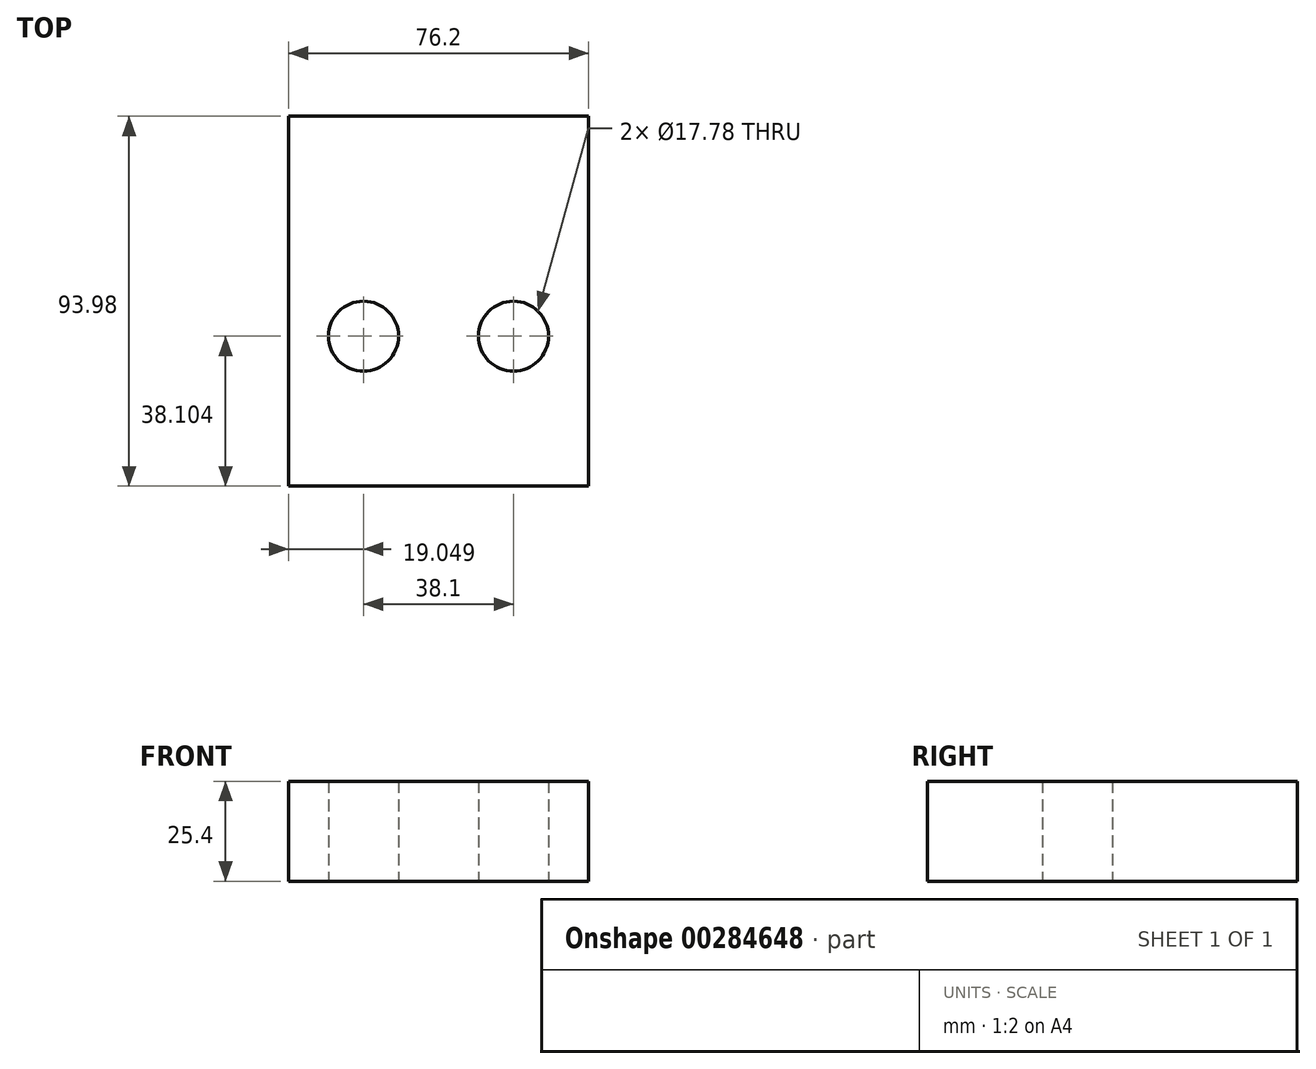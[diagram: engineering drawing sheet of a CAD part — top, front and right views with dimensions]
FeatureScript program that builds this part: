
annotation { "Feature Type Name" : "Feature", "Feature Type Description" : "" }
export const myFeature = defineFeature(function(context is Context, id is Id, definition is map)
    precondition{}
    {
        {
            var Q0;
            Q0=qCreatedBy(makeId("Top.planeOp"),FACE);
            var sketch = newSketch(context, id + "F0", { "sketchPlane" : qUnion([Q0])});
            skLineSegment(sketch, "E0", {"start": v(-41.9, 19.86) * mm, "end": v(-41.9, -56.34) * mm});
            skLineSegment(sketch, "E1", {"start": v(-41.9, -56.34) * mm, "end": v(34.3, -56.34) * mm});
            skLineSegment(sketch, "E2", {"start": v(34.3, -56.34) * mm, "end": v(34.3, 19.86) * mm});
            skLineSegment(sketch, "E3", {"start": v(34.3, 19.86) * mm, "end": v(-41.9, 19.86) * mm});
            skLineSegment(sketch, "E4", {"start": v(34.3, 19.86) * mm, "end": v(34.3, 37.64) * mm});
            skLineSegment(sketch, "E5", {"start": v(34.3, 37.64) * mm, "end": v(-41.9, 37.64) * mm});
            skLineSegment(sketch, "E6", {"start": v(-41.9, 37.64) * mm, "end": v(-41.9, 19.86) * mm});
            skPoint(sketch, "E7.endSnap0", {"position": v(34.3, -18.24) * mm});
            skCircle(sketch, "E8", {"center": v(-22.84, -18.24) * mm, "radius": 8.9 * mm});
            skCircle(sketch, "E9", {"center": v(15.26, -18.24) * mm, "radius": 8.9 * mm});
            skPoint(sketch, "E7.start.orphan", {"position": v(34.3, -18.24) * mm});
            skSolve(sketch);
        }
        {
            var Q0;
            Q0 = qSketchRegion(id + "F0", true);
            extrude(context, id + "F1", {"entities" : qUnion([Q0]), "depth" : 25.4 * mm});
        }
    });
